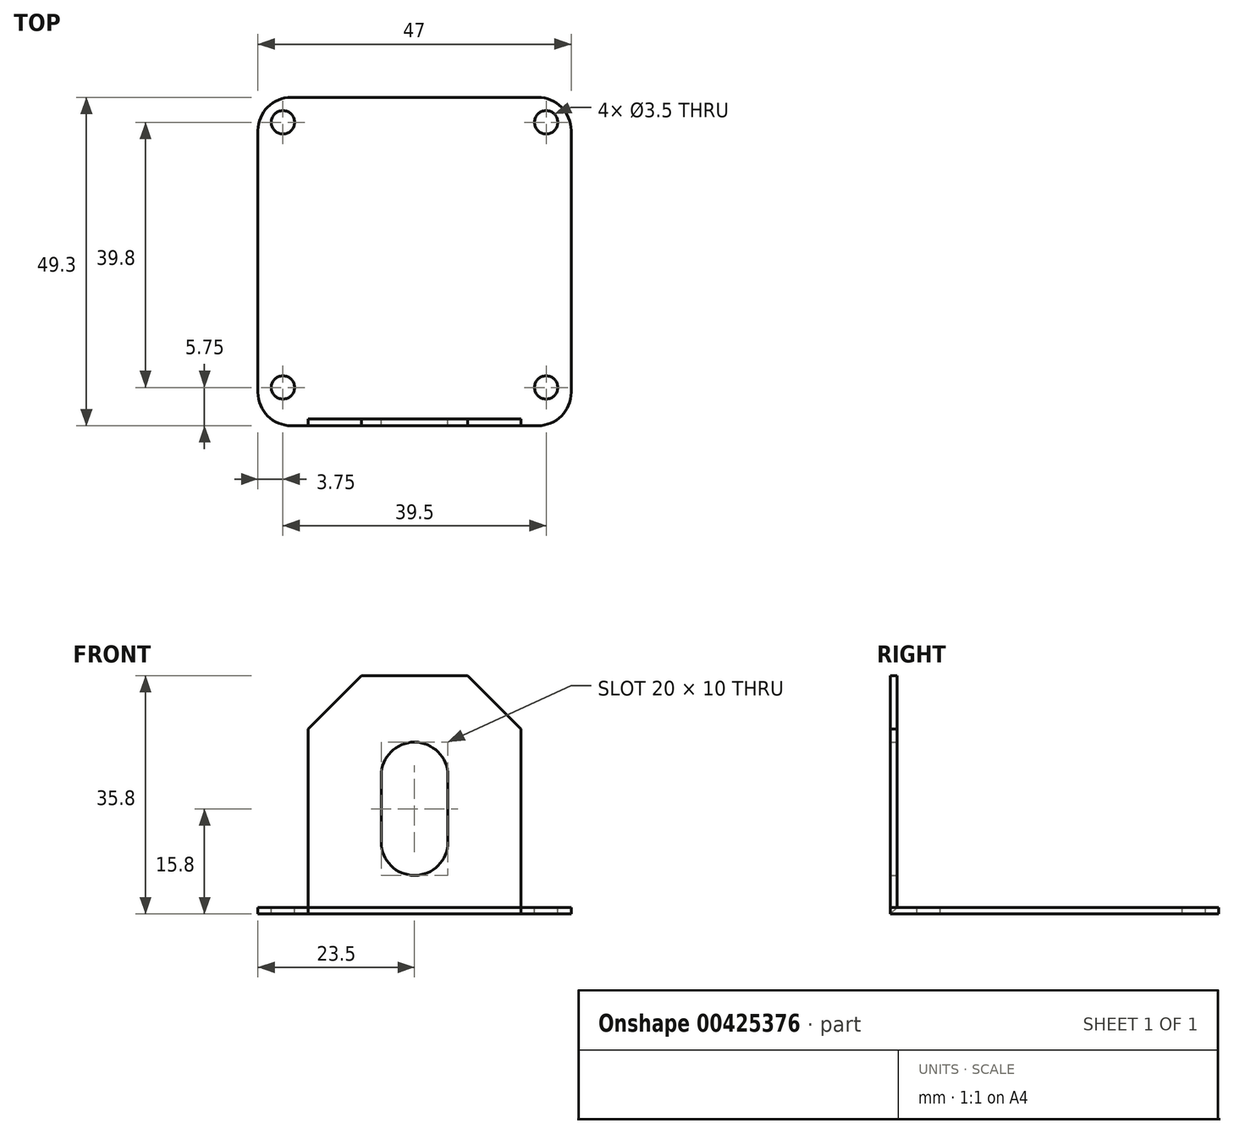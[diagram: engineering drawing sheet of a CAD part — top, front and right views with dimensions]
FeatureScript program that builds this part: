
annotation { "Feature Type Name" : "Feature", "Feature Type Description" : "" }
export const myFeature = defineFeature(function(context is Context, id is Id, definition is map)
    precondition{}
    {
        {
            var Q0;
            Q0=qCreatedBy(makeId("Right.planeOp"),FACE);
            var sketch = newSketch(context, id + "F0", { "sketchPlane" : qUnion([Q0])});
            skLineSegment(sketch, "E0", {"start": v(-1, 20) * mm, "end": v(-1, -15.8) * mm});
            skLineSegment(sketch, "E1", {"start": v(-1, -15.8) * mm, "end": v(48.3, -15.8) * mm, "construction": true});
            skLineSegment(sketch, "E2", {"start": v(48.3, -15.8) * mm, "end": v(48.3, -14.8) * mm, "construction": true});
            skLineSegment(sketch, "E3", {"start": v(48.3, -14.8) * mm, "end": v(0, -14.8) * mm, "construction": true});
            skLineSegment(sketch, "E4", {"start": v(0, -14.8) * mm, "end": v(0, 20) * mm});
            skLineSegment(sketch, "E5", {"start": v(0, 20) * mm, "end": v(-1, 20) * mm});
            skLineSegment(sketch, "E6", {"start": v(0, -14.8) * mm, "end": v(-1, -15.8) * mm});
            skSolve(sketch);
        }
        {
            var Q0;
            Q0 = qSketchRegion(id + "F0", true);
            extrude(context, id + "F1", {"entities" : qUnion([Q0]), "depth" : 16 * mm, "hasSecondDirection" : true, "secondDirectionOppositeDirection" : true, "secondDirectionDepth" : 16 * mm});
        }
        {
            var Q0;
            Q0=qCreatedBy(makeId("Right.planeOp"),FACE);
            var sketch = newSketch(context, id + "F2", { "sketchPlane" : qUnion([Q0])});
            skLineSegment(sketch, "E7.bottom", {"start": v(48.3, -14.8) * mm, "end": v(-1, -14.8) * mm});
            skLineSegment(sketch, "E7.top", {"start": v(48.3, -15.8) * mm, "end": v(-1, -15.8) * mm});
            skLineSegment(sketch, "E7.left", {"start": v(48.3, -15.8) * mm, "end": v(48.3, -14.8) * mm});
            skLineSegment(sketch, "E7.right", {"start": v(-1, -15.8) * mm, "end": v(-1, -14.8) * mm});
            skSolve(sketch);
        }
        {
            var Q0;
            Q0 = qSketchRegion(id + "F2", true);
            extrude(context, id + "F3", {"entities" : qUnion([Q0]), "depth" : 23.5 * mm, "hasSecondDirection" : true, "secondDirectionOppositeDirection" : true, "secondDirectionDepth" : 23.5 * mm});
        }
        {
            var Q0;
            Q0=qCreatedBy(makeId("Front.planeOp"),FACE);
            var sketch = newSketch(context, id + "F4", { "sketchPlane" : qUnion([Q0])});
            skArc(sketch, "E8", {"start": v(5, 5) * mm, "mid": v(0, 10) * mm, "end": v(-5, 5) * mm});
            skLineSegment(sketch, "E9", {"start": v(-5, 5) * mm, "end": v(-5, -5) * mm});
            skLineSegment(sketch, "E10", {"start": v(5, 5) * mm, "end": v(5, -5) * mm});
            skArc(sketch, "E11", {"start": v(-5, -5) * mm, "mid": v(0, -10) * mm, "end": v(5, -5) * mm});
            skLineSegment(sketch, "E12", {"start": v(0, 5) * mm, "end": v(0, -5) * mm, "construction": true});
            skSolve(sketch);
        }
        {
            var Q0;
            Q0=makeQuery(id+"F1.opExtrude","CAP_EDGE",EDGE,{"disambiguationData":[OSD([sQuery(id+"F0.wireOp",EDGE,"E5")])],"isStart":true});
            var Q1;
            Q1=makeQuery(id+"F1.opExtrude","CAP_EDGE",EDGE,{"disambiguationData":[OSD([sQuery(id+"F0.wireOp",EDGE,"E5")])],"isStart":false});
            chamfer(context, id + "F5", {"entities" : qUnion([Q0, Q1]), "width" : 8 * mm, "tangentPropagation" : true});
        }
        {
            var Q0;
            Q0 = qSketchRegion(id + "F4", true);
            extrude(context, id + "F6", {"entities" : qUnion([Q0]), "operationType" : NewBodyOperationType.REMOVE, "depth" : 5 * mm});
        }
        {
            var Q0;
            Q0=makeQuery(id+"F3.opExtrude","CAP_EDGE",EDGE,{"disambiguationData":[OSD([sQuery(id+"F2.wireOp",EDGE,"E7.left")])],"isStart":false});
            var Q1;
            Q1=makeQuery(id+"F3.opExtrude","CAP_EDGE",EDGE,{"disambiguationData":[OSD([sQuery(id+"F2.wireOp",EDGE,"E7.left")])],"isStart":true});
            var Q2;
            Q2=makeQuery(id+"F3.opExtrude","CAP_EDGE",EDGE,{"disambiguationData":[OSD([sQuery(id+"F2.wireOp",EDGE,"E7.right")])],"isStart":false});
            var Q3;
            Q3=makeQuery(id+"F3.opExtrude","CAP_EDGE",EDGE,{"disambiguationData":[OSD([sQuery(id+"F2.wireOp",EDGE,"E7.right")])],"isStart":true});
            fillet(context, id + "F7", {"entities" : qUnion([Q0, Q1, Q2, Q3]), "radius" : 5 * mm, "tangentPropagation" : true, "allowEdgeOverflow" : false});
        }
        {
            var Q0;
            Q0=makeQuery(id+"F3.opExtrude","SWEPT_FACE",FACE,{"disambiguationData":[OSD([sQuery(id+"F2.wireOp",EDGE,"E7.bottom")])]});
            var sketch = newSketch(context, id + "F8", { "sketchPlane" : qUnion([Q0])});
            skLineSegment(sketch, "E13.bottom", {"start": v(19.75, 4.75) * mm, "end": v(-19.75, 4.75) * mm, "construction": true});
            skLineSegment(sketch, "E13.top", {"start": v(19.75, 44.55) * mm, "end": v(-19.75, 44.55) * mm, "construction": true});
            skLineSegment(sketch, "E13.left", {"start": v(19.75, 4.75) * mm, "end": v(19.75, 44.55) * mm, "construction": true});
            skLineSegment(sketch, "E13.right", {"start": v(-19.75, 4.75) * mm, "end": v(-19.75, 44.55) * mm, "construction": true});
            skCircle(sketch, "E14", {"center": v(-19.75, 44.55) * mm, "radius": 1.75 * mm});
            skCircle(sketch, "E15", {"center": v(-19.75, 4.75) * mm, "radius": 1.75 * mm});
            skCircle(sketch, "E16", {"center": v(19.75, 4.75) * mm, "radius": 1.75 * mm});
            skCircle(sketch, "E17", {"center": v(19.75, 44.55) * mm, "radius": 1.75 * mm});
            skSolve(sketch);
        }
        {
            var Q0;
            Q0 = qSketchRegion(id + "F8", true);
            extrude(context, id + "F9", {"entities" : qUnion([Q0]), "operationType" : NewBodyOperationType.REMOVE, "oppositeDirection" : true, "depth" : 25 * mm});
        }
    });
